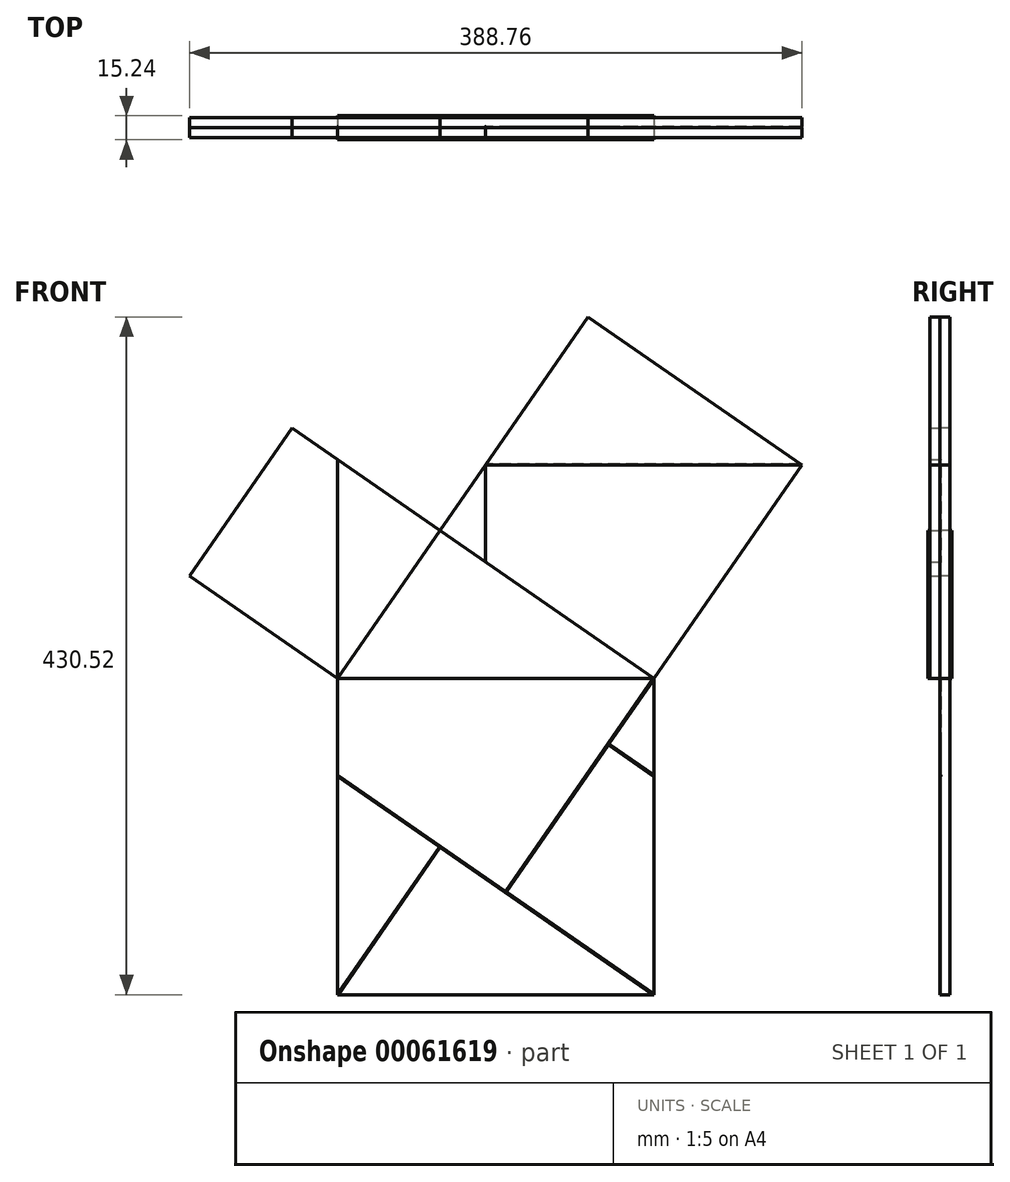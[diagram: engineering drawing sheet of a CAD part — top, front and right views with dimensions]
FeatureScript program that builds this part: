
annotation { "Feature Type Name" : "Feature", "Feature Type Description" : "" }
export const myFeature = defineFeature(function(context is Context, id is Id, definition is map)
    precondition{}
    {
        {
            var Q0;
            Q0=qCreatedBy(makeId("Front.planeOp"),FACE);
            var sketch = newSketch(context, id + "F0", { "sketchPlane" : qUnion([Q0])});
            skLineSegment(sketch, "E0", {"start": v(0, 0) * mm, "end": v(-65.06, -93.98) * mm});
            skLineSegment(sketch, "E1", {"start": v(0, 0) * mm, "end": v(135.74, -93.98) * mm});
            skLineSegment(sketch, "E2", {"start": v(135.74, -93.98) * mm, "end": v(-65.06, -93.98) * mm});
            skLineSegment(sketch, "E3", {"start": v(93.98, 135.74) * mm, "end": v(229.72, 41.77) * mm});
            skLineSegment(sketch, "E4", {"start": v(229.72, 41.77) * mm, "end": v(135.74, -93.98) * mm});
            skLineSegment(sketch, "E5", {"start": v(0, 0) * mm, "end": v(-93.98, 65.06) * mm});
            skLineSegment(sketch, "E6", {"start": v(-93.98, 65.06) * mm, "end": v(-159.04, -28.92) * mm});
            skLineSegment(sketch, "E7", {"start": v(-159.04, -28.92) * mm, "end": v(-65.06, -93.98) * mm});
            skLineSegment(sketch, "E8", {"start": v(-65.06, -93.98) * mm, "end": v(-65.06, -294.78) * mm});
            skLineSegment(sketch, "E9", {"start": v(-65.06, -294.78) * mm, "end": v(135.74, -294.78) * mm});
            skLineSegment(sketch, "E10", {"start": v(135.74, -294.78) * mm, "end": v(135.74, -93.98) * mm});
            skLineSegment(sketch, "E11", {"start": v(0, 0) * mm, "end": v(93.98, 135.74) * mm});
            skLineSegment(sketch, "E12", {"start": v(229.72, 41.77) * mm, "end": v(28.92, 41.77) * mm});
            skLineSegment(sketch, "E13", {"start": v(28.92, 41.77) * mm, "end": v(28.92, -20.02) * mm});
            skLineSegment(sketch, "E14", {"start": v(-65.06, -93.98) * mm, "end": v(-65.06, 45.04) * mm});
            skLineSegment(sketch, "E15", {"start": v(135.74, -93.98) * mm, "end": v(41.77, -229.72) * mm});
            skLineSegment(sketch, "E16", {"start": v(-65.06, -294.78) * mm, "end": v(0, -200.8) * mm});
            skLineSegment(sketch, "E17", {"start": v(-65.06, -155.76) * mm, "end": v(135.74, -294.78) * mm});
            skLineSegment(sketch, "E18", {"start": v(106.83, -135.74) * mm, "end": v(135.74, -155.76) * mm});
            skLineSegment(sketch, "E19", {"start": v(135.74, -93.98) * mm, "end": v(135.74, -155.76) * mm});
            skSolve(sketch);
        }
        {
            var Q0;
            {var subQ0=sQuery(id+"F0.wireOp",EDGE,"E0");Q0=makeQuery(id+"F0.imprint","IMPRINT",FACE,{"disambiguationData":[TD([[makeQuery(id+"F0.imprint","IMPRINT",EDGE,{"derivedFrom":subQ0}),1.0]])]});}
            extrude(context, id + "F1", {"entities" : qUnion([Q0]), "oppositeDirection" : true, "depth" : 15.24 * mm, "symmetric" : true});
        }
        {
            var Q0;
            {var subQ0=sQuery(id+"F0.wireOp",EDGE,"E4");Q0=makeQuery(id+"F0.imprint","IMPRINT",FACE,{"disambiguationData":[TD([[makeQuery(id+"F0.imprint","IMPRINT",EDGE,{"derivedFrom":subQ0}),-1.0]])]});}
            var Q1;
            {var subQ0=sQuery(id+"F0.wireOp",EDGE,"E0");Q1=makeQuery(id+"F0.imprint","IMPRINT",FACE,{"disambiguationData":[TD([[makeQuery(id+"F0.imprint","IMPRINT",EDGE,{"derivedFrom":subQ0}),-1.0]])]});}
            extrude(context, id + "F2", {"entities" : qUnion([Q0, Q1]), "depth" : 6.35 * mm});
        }
        {
            var Q0;
            {var subQ0=sQuery(id+"F0.wireOp",EDGE,"E3");Q0=makeQuery(id+"F0.imprint","IMPRINT",FACE,{"disambiguationData":[TD([[makeQuery(id+"F0.imprint","IMPRINT",EDGE,{"derivedFrom":subQ0}),-1.0]])]});}
            var Q1;
            {var subQ0=sQuery(id+"F0.wireOp",EDGE,"E6");Q1=makeQuery(id+"F0.imprint","IMPRINT",FACE,{"disambiguationData":[TD([[makeQuery(id+"F0.imprint","IMPRINT",EDGE,{"derivedFrom":subQ0}),1.0]])]});}
            var Q2;
            {var subQ3=sQuery(id+"F0.wireOp",EDGE,"E13");Q2=makeQuery(id+"F0.imprint","IMPRINT",FACE,{"disambiguationData":[TD([[makeQuery(id+"F0.imprint","IMPRINT",EDGE,{"derivedFrom":subQ3}),-1.0]])]});}
            extrude(context, id + "F3", {"entities" : qUnion([Q0, Q1, Q2]), "depth" : 6.35 * mm});
        }
        {
            var Q0;
            Q0 = qSketchRegion(id + "F0", true);
            extrude(context, id + "F4", {"entities" : qUnion([Q0]), "oppositeDirection" : true, "depth" : 6.35 * mm});
        }
        {
            var Q0;
            {var subQ4=sQuery(id+"F0.wireOp",EDGE,"E2");Q0=makeQuery(id+"F0.imprint","IMPRINT",FACE,{"disambiguationData":[TD([[makeQuery(id+"F0.imprint","IMPRINT",EDGE,{"derivedFrom":subQ4}),1.0]])]});}
            var sketch = newSketch(context, id + "F5", { "sketchPlane" : qUnion([Q0])});
            skLineSegment(sketch, "E20.KFFB.KFFB", {"start": v(-65.06, -155.76) * mm, "end": v(135.74, -294.78) * mm, "construction": true});
            skLineSegment(sketch, "E20.JF9.JF9", {"start": v(135.74, -93.98) * mm, "end": v(41.77, -229.72) * mm, "construction": true});
            skLineSegment(sketch, "E20.KFJB.KFJB", {"start": v(106.83, -135.74) * mm, "end": v(135.74, -155.76) * mm, "construction": true});
            skLineSegment(sketch, "E20.KFBB.KFBB", {"start": v(-65.06, -294.78) * mm, "end": v(0, -200.8) * mm, "construction": true});
            skArc(sketch, "E20.0.startCap", {"start": v(-65.28, -156.08) * mm, "mid": v(-65.37, -155.55) * mm, "end": v(-64.84, -155.45) * mm});
            skArc(sketch, "E20.0.endCap", {"start": v(135.96, -294.47) * mm, "mid": v(136.06, -295) * mm, "end": v(135.53, -295.1) * mm});
            skLineSegment(sketch, "E20.0.left", {"start": v(-64.84, -155.45) * mm, "end": v(135.96, -294.47) * mm});
            skLineSegment(sketch, "E20.0.right", {"start": v(-65.28, -156.08) * mm, "end": v(135.53, -295.1) * mm});
            skArc(sketch, "E20.1.startCap", {"start": v(135.43, -93.76) * mm, "mid": v(135.96, -93.66) * mm, "end": v(136.06, -94.2) * mm});
            skArc(sketch, "E20.1.endCap", {"start": v(42.08, -229.94) * mm, "mid": v(41.55, -230.03) * mm, "end": v(41.45, -229.5) * mm});
            skLineSegment(sketch, "E20.1.left", {"start": v(136.06, -94.2) * mm, "end": v(42.08, -229.94) * mm});
            skLineSegment(sketch, "E20.1.right", {"start": v(135.43, -93.76) * mm, "end": v(41.45, -229.5) * mm});
            skArc(sketch, "E20.2.startCap", {"start": v(106.61, -136.06) * mm, "mid": v(106.51, -135.53) * mm, "end": v(107.04, -135.43) * mm});
            skArc(sketch, "E20.2.endCap", {"start": v(135.96, -155.45) * mm, "mid": v(136.06, -155.98) * mm, "end": v(135.53, -156.08) * mm});
            skLineSegment(sketch, "E20.2.left", {"start": v(107.04, -135.43) * mm, "end": v(135.96, -155.45) * mm});
            skLineSegment(sketch, "E20.2.right", {"start": v(106.61, -136.06) * mm, "end": v(135.53, -156.08) * mm});
            skArc(sketch, "E20.3.startCap", {"start": v(-64.75, -295) * mm, "mid": v(-65.28, -295.1) * mm, "end": v(-65.37, -294.56) * mm});
            skArc(sketch, "E20.3.endCap", {"start": v(-0.31, -200.59) * mm, "mid": v(0.22, -200.5) * mm, "end": v(0.31, -201.02) * mm});
            skLineSegment(sketch, "E20.3.left", {"start": v(-65.37, -294.56) * mm, "end": v(-0.31, -200.59) * mm});
            skLineSegment(sketch, "E20.3.right", {"start": v(-64.75, -295) * mm, "end": v(0.31, -201.02) * mm});
            skLineSegment(sketch, "E21.JF5.JF5", {"start": v(-65.06, -93.98) * mm, "end": v(-65.06, 45.04) * mm, "construction": true});
            skLineSegment(sketch, "E21.JF1.JF1", {"start": v(28.92, 41.77) * mm, "end": v(28.92, -20.02) * mm, "construction": true});
            skLineSegment(sketch, "E21.JFx.JFx", {"start": v(229.72, 41.77) * mm, "end": v(28.92, 41.77) * mm, "construction": true});
            skArc(sketch, "E21.0.startCap", {"start": v(-64.68, -93.98) * mm, "mid": v(-65.06, -94.36) * mm, "end": v(-65.44, -93.98) * mm});
            skArc(sketch, "E21.0.endCap", {"start": v(-65.44, 45.04) * mm, "mid": v(-65.06, 45.42) * mm, "end": v(-64.68, 45.04) * mm});
            skLineSegment(sketch, "E21.0.left", {"start": v(-65.44, -93.98) * mm, "end": v(-65.44, 45.04) * mm});
            skLineSegment(sketch, "E21.0.right", {"start": v(-64.68, -93.98) * mm, "end": v(-64.68, 45.04) * mm});
            skArc(sketch, "E21.1.startCap", {"start": v(28.53, 41.77) * mm, "mid": v(28.92, 42.15) * mm, "end": v(29.3, 41.77) * mm});
            skArc(sketch, "E21.1.endCap", {"start": v(29.3, -20.02) * mm, "mid": v(28.92, -20.4) * mm, "end": v(28.53, -20.02) * mm});
            skLineSegment(sketch, "E21.1.left", {"start": v(29.3, 41.77) * mm, "end": v(29.3, -20.02) * mm});
            skLineSegment(sketch, "E21.1.right", {"start": v(28.53, 41.77) * mm, "end": v(28.53, -20.02) * mm});
            skArc(sketch, "E21.2.startCap", {"start": v(229.72, 42.15) * mm, "mid": v(230.1, 41.77) * mm, "end": v(229.72, 41.39) * mm});
            skArc(sketch, "E21.2.endCap", {"start": v(28.92, 41.39) * mm, "mid": v(28.53, 41.77) * mm, "end": v(28.92, 42.15) * mm});
            skLineSegment(sketch, "E21.2.left", {"start": v(229.72, 41.39) * mm, "end": v(28.92, 41.39) * mm});
            skLineSegment(sketch, "E21.2.right", {"start": v(229.72, 42.15) * mm, "end": v(28.92, 42.15) * mm});
            skSolve(sketch);
        }
        {
            var Q0;
            Q0 = qSketchRegion(id + "F5", true);
            extrude(context, id + "F6", {"entities" : qUnion([Q0]), "operationType" : NewBodyOperationType.REMOVE, "oppositeDirection" : true, "depth" : 0.76 * mm});
        }
    });
